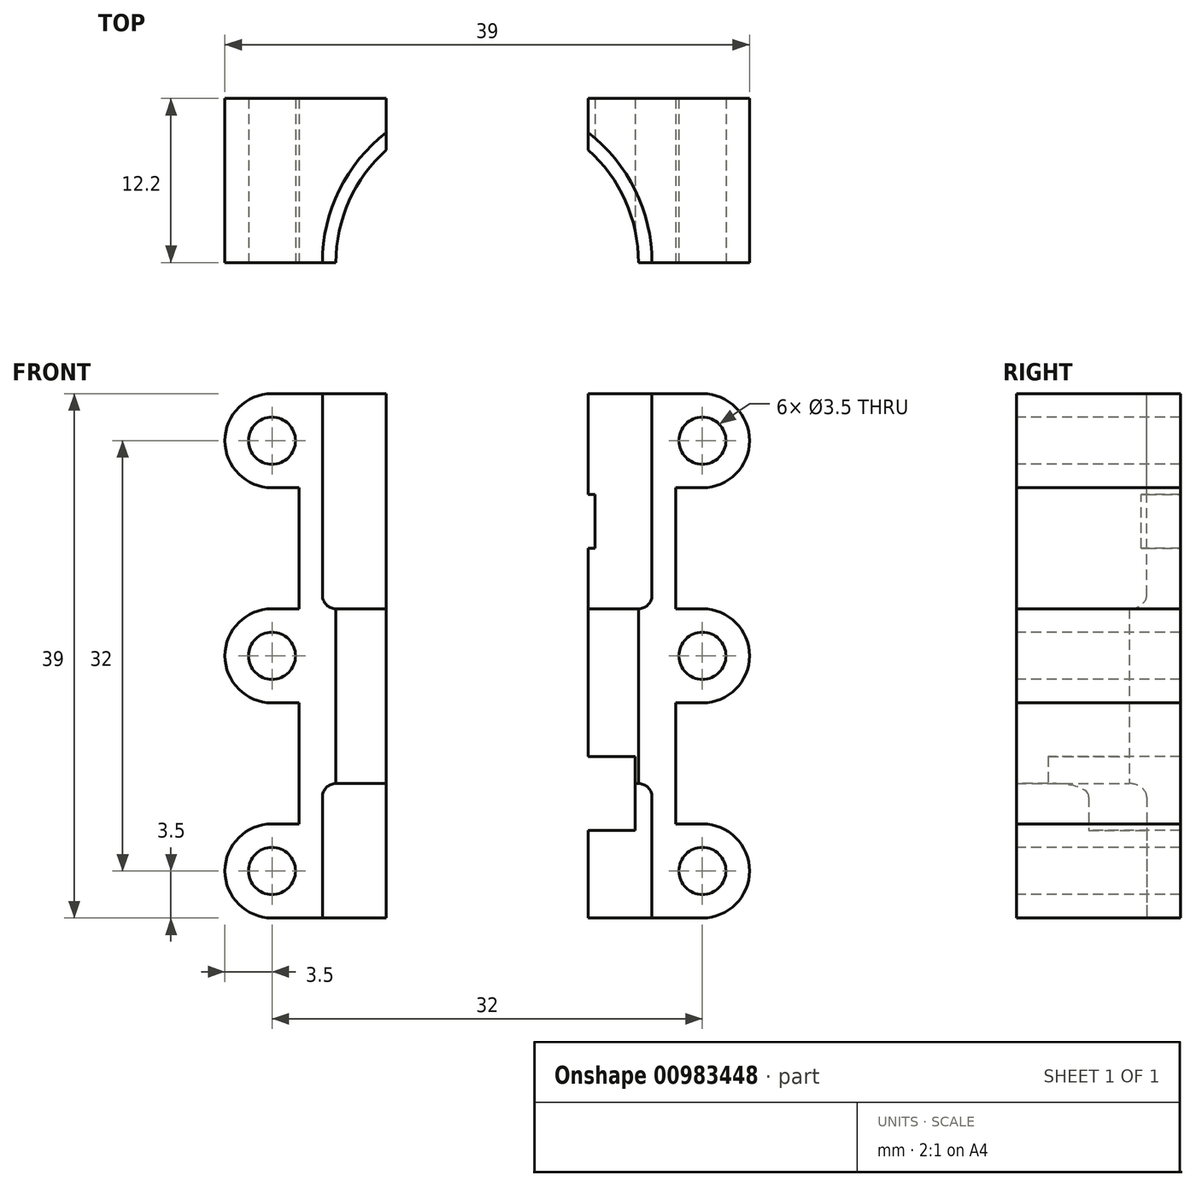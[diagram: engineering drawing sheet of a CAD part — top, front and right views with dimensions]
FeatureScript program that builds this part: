
annotation { "Feature Type Name" : "Feature", "Feature Type Description" : "" }
export const myFeature = defineFeature(function(context is Context, id is Id, definition is map)
    precondition{}
    {
        {
            var Q0;
            Q0=qCreatedBy(makeId("Top.planeOp"),FACE);
            var sketch = newSketch(context, id + "F0", { "sketchPlane" : qUnion([Q0])});
            skCircle(sketch, "E0", {"center": v(0, 0) * mm, "radius": 11.25 * mm});
            skSolve(sketch);
        }
        {
            var Q0;
            Q0=qSketchRegion(id+"F0",true);
            extrude(context, id + "F1", {"entities" : qUnion([Q0]), "depth" : 39 * mm, "offsetDistance" : 25 * mm});
        }
        {
            var Q0;
            Q0=makeQuery(id+"F1.opExtrude","CAP_FACE",FACE,{"disambiguationData":[OSD([sQuery(id+"F0.wireOp",EDGE,"E0")])],"isStart":false});
            var sketch = newSketch(context, id + "F2", { "sketchPlane" : qUnion([Q0])});
            skCircle(sketch, "E1", {"center": v(0, 0) * mm, "radius": 12.25 * mm});
            skSolve(sketch);
        }
        {
            var Q0;
            Q0=makeQuery(id+"F2.imprint","IMPRINT",FACE,{"disambiguationData":[TD([[makeQuery(id+"F2.imprint","IMPRINT",EDGE,{"derivedFrom":sQuery(id+"F2.wireOp",EDGE,"E1")}),1.0]])]});
            extrude(context, id + "F3", {"entities" : qUnion([Q0]), "operationType" : NewBodyOperationType.ADD, "oppositeDirection" : true, "depth" : 16 * mm, "offsetDistance" : 25 * mm});
        }
        {
            var Q0;
            Q0=makeQuery(id+"F1.opExtrude","CAP_FACE",FACE,{"disambiguationData":[OSD([sQuery(id+"F0.wireOp",EDGE,"E0")])],"isStart":true});
            var sketch = newSketch(context, id + "F4", { "sketchPlane" : qUnion([Q0])});
            skCircle(sketch, "E2", {"center": v(0, 0) * mm, "radius": 12.25 * mm});
            skSolve(sketch);
        }
        {
            var Q0;
            Q0=makeQuery(id+"F3.opExtrude","CAP_EDGE",EDGE,{"disambiguationData":[OSD([sQuery(id+"F2.wireOp",EDGE,"E1")])],"isStart":false});
            fillet(context, id + "F5", {"entities" : qUnion([Q0]), "radius" : 1 * mm, "tangentPropagation" : true, "allowEdgeOverflow" : false});
        }
        {
            var Q0;
            Q0=makeQuery(id+"F4.imprint","IMPRINT",FACE,{"disambiguationData":[TD([[makeQuery(id+"F4.imprint","IMPRINT",EDGE,{"derivedFrom":sQuery(id+"F4.wireOp",EDGE,"E2")}),1.0]])]});
            extrude(context, id + "F6", {"entities" : qUnion([Q0]), "operationType" : NewBodyOperationType.ADD, "oppositeDirection" : true, "depth" : 10 * mm, "offsetDistance" : 25 * mm});
        }
        {
            var Q0;
            Q0=makeQuery(id+"F6.opExtrude","CAP_EDGE",EDGE,{"disambiguationData":[OSD([sQuery(id+"F4.wireOp",EDGE,"E2")])],"isStart":false});
            fillet(context, id + "F7", {"entities" : qUnion([Q0]), "radius" : 1 * mm, "tangentPropagation" : true, "allowEdgeOverflow" : false});
        }
        {
            var Q0;
            {var subQ0=sQuery(id+"F0.wireOp",EDGE,"E0");Q0=makeQuery(id+"F6.boolean.opBoolean","MERGE",FACE,{"derivedFrom":[makeQuery(id+"F1.opExtrude","CAP_FACE",FACE,{"disambiguationData":[OSD([subQ0])],"isStart":true}),makeQuery(id+"F6.opExtrude","CAP_FACE",FACE,{"disambiguationData":[OSD([subQ0,sQuery(id+"F4.wireOp",EDGE,"E2")])],"isStart":true})]});}
            var sketch = newSketch(context, id + "F8", { "sketchPlane" : qUnion([Q0])});
            skLineSegment(sketch, "E3.bottom", {"start": v(-5.5, 12.25) * mm, "end": v(5.5, 12.25) * mm});
            skLineSegment(sketch, "E3.top", {"start": v(-5.5, 10.25) * mm, "end": v(5.5, 10.25) * mm});
            skLineSegment(sketch, "E3.left", {"start": v(-5.5, 12.25) * mm, "end": v(-5.5, 10.25) * mm});
            skLineSegment(sketch, "E3.right", {"start": v(5.5, 12.25) * mm, "end": v(5.5, 10.25) * mm});
            skPoint(sketch, "E3.middle", {"position": v(0, 11.25) * mm});
            skSolve(sketch);
        }
        {
            var Q0;
            {var subQ0=sQuery(id+"F8.wireOp",EDGE,"E3.left");var subQ1=sQuery(id+"F8.wireOp",EDGE,"E3.bottom");var subQ2=makeQuery(id+"F8.imprint","INTERSECT",VERTEX,{"derivedFrom":[subQ1,subQ0]});Q0=makeQuery(id+"F8.imprint","IMPRINT",FACE,{"disambiguationData":[TD([[makeQuery(id+"F8.imprint","IMPRINT",EDGE,{"disambiguationData":[TD([[subQ2,-1.0]])],"derivedFrom":subQ1}),-1.0]])]});}
            var Q1;
            {var subQ0=sQuery(id+"F8.wireOp",EDGE,"E3.right");var subQ1=sQuery(id+"F8.wireOp",EDGE,"E3.bottom");var subQ2=makeQuery(id+"F8.imprint","INTERSECT",VERTEX,{"derivedFrom":[subQ1,subQ0]});Q1=makeQuery(id+"F8.imprint","IMPRINT",FACE,{"disambiguationData":[TD([[makeQuery(id+"F8.imprint","IMPRINT",EDGE,{"disambiguationData":[TD([[subQ2,1.0]])],"derivedFrom":subQ1}),-1.0]])]});}
            extrude(context, id + "F9", {"entities" : qUnion([Q0, Q1]), "operationType" : NewBodyOperationType.ADD, "oppositeDirection" : true, "depth" : 9 * mm, "offsetDistance" : 25 * mm});
        }
        {
            var Q0;
            {var subQ0=sQuery(id+"F8.wireOp",EDGE,"E3.bottom");var subQ1=sQuery(id+"F4.wireOp",EDGE,"E2");var subQ2=sQuery(id+"F0.wireOp",EDGE,"E0");Q0=makeQuery(id+"F9.boolean.opBoolean","MERGE",FACE,{"derivedFrom":[makeQuery(id+"F6.boolean.opBoolean","MERGE",FACE,{"derivedFrom":[makeQuery(id+"F1.opExtrude","CAP_FACE",FACE,{"disambiguationData":[OSD([subQ2])],"isStart":true}),makeQuery(id+"F6.opExtrude","CAP_FACE",FACE,{"disambiguationData":[OSD([subQ2,subQ1])],"isStart":true})]}),makeQuery(id+"F9.opExtrude","CAP_FACE",FACE,{"disambiguationData":[OSD([subQ1,subQ0,sQuery(id+"F8.wireOp",EDGE,"E3.left")])],"isStart":true}),makeQuery(id+"F9.opExtrude","CAP_FACE",FACE,{"disambiguationData":[OSD([subQ1,subQ0,sQuery(id+"F8.wireOp",EDGE,"E3.right")])],"isStart":true})]});}
            var sketch = newSketch(context, id + "F10", { "sketchPlane" : qUnion([Q0])});
            skLineSegment(sketch, "E4.bottom", {"start": v(-7.5, -8.25) * mm, "end": v(7.5, -8.25) * mm});
            skLineSegment(sketch, "E4.top", {"start": v(-7.5, -12.25) * mm, "end": v(7.5, -12.25) * mm});
            skLineSegment(sketch, "E4.left", {"start": v(-7.5, -8.25) * mm, "end": v(-7.5, -12.25) * mm});
            skLineSegment(sketch, "E4.right", {"start": v(7.5, -8.25) * mm, "end": v(7.5, -12.25) * mm});
            skPoint(sketch, "E4.middle", {"position": v(0, -10.25) * mm});
            skSolve(sketch);
        }
        {
            var Q0;
            {var subQ0=sQuery(id+"F10.wireOp",EDGE,"E4.right");var subQ1=sQuery(id+"F10.wireOp",EDGE,"E4.top");var subQ2=makeQuery(id+"F10.imprint","INTERSECT",VERTEX,{"derivedFrom":[subQ1,subQ0]});Q0=makeQuery(id+"F10.imprint","IMPRINT",FACE,{"disambiguationData":[TD([[makeQuery(id+"F10.imprint","IMPRINT",EDGE,{"disambiguationData":[TD([[subQ2,1.0]])],"derivedFrom":subQ1}),1.0]])]});}
            var Q1;
            {var subQ0=sQuery(id+"F10.wireOp",EDGE,"E4.left");var subQ1=sQuery(id+"F10.wireOp",EDGE,"E4.top");var subQ2=makeQuery(id+"F10.imprint","INTERSECT",VERTEX,{"derivedFrom":[subQ1,subQ0]});Q1=makeQuery(id+"F10.imprint","IMPRINT",FACE,{"disambiguationData":[TD([[makeQuery(id+"F10.imprint","IMPRINT",EDGE,{"disambiguationData":[TD([[subQ2,-1.0]])],"derivedFrom":subQ1}),1.0]])]});}
            var Q2;
            {var subQ4=sQuery(id+"F10.wireOp",EDGE,"E4.bottom");Q2=makeQuery(id+"F10.imprint","IMPRINT",FACE,{"disambiguationData":[TD([[makeQuery(id+"F10.imprint","IMPRINT",EDGE,{"derivedFrom":subQ4}),-1.0]])]});}
            extrude(context, id + "F11", {"entities" : qUnion([Q0, Q1, Q2]), "operationType" : NewBodyOperationType.ADD, "oppositeDirection" : true, "depth" : 39 * mm, "offsetDistance" : 25 * mm});
        }
        {
            var Q0;
            Q0=makeQuery(id+"F11.opExtrude","SWEPT_FACE",FACE,{"disambiguationData":[OSD([sQuery(id+"F10.wireOp",EDGE,"E4.top")])]});
            var sketch = newSketch(context, id + "F12", { "sketchPlane" : qUnion([Q0])});
            skLineSegment(sketch, "E5.bottom", {"start": v(-11, 12) * mm, "end": v(-7.5, 12) * mm});
            skLineSegment(sketch, "E5.top", {"start": v(-11, 6.5) * mm, "end": v(-7.5, 6.5) * mm});
            skLineSegment(sketch, "E5.left", {"start": v(-11, 12) * mm, "end": v(-11, 6.5) * mm});
            skLineSegment(sketch, "E5.right", {"start": v(-7.5, 12) * mm, "end": v(-7.5, 6.5) * mm});
            skSolve(sketch);
        }
        {
            var Q0;
            Q0=makeQuery(id+"F12.imprint","IMPRINT",FACE,{"disambiguationData":[TD([[makeQuery(id+"F12.imprint","IMPRINT",EDGE,{"derivedFrom":sQuery(id+"F12.wireOp",EDGE,"E5.bottom")}),-1.0]])]});
            extrude(context, id + "F13", {"entities" : qUnion([Q0]), "operationType" : NewBodyOperationType.ADD, "depth" : 2 * mm, "offsetDistance" : 25 * mm, "hasSecondDirection" : true, "secondDirectionOppositeDirection" : true, "secondDirectionDepth" : 12 * mm});
        }
        {
            var Q0;
            Q0=makeQuery(id+"F11.opExtrude","SWEPT_FACE",FACE,{"disambiguationData":[OSD([sQuery(id+"F10.wireOp",EDGE,"E4.top")])]});
            var sketch = newSketch(context, id + "F14", { "sketchPlane" : qUnion([Q0])});
            skCircle(sketch, "E6", {"center": v(-0.06, 19) * mm, "radius": 6.5 * mm});
            skSolve(sketch);
        }
        {
            var Q0;
            Q0=makeQuery(id+"F14.imprint","IMPRINT",FACE,{"disambiguationData":[TD([[makeQuery(id+"F14.imprint","IMPRINT",EDGE,{"derivedFrom":sQuery(id+"F14.wireOp",EDGE,"E6")}),1.0]])]});
            extrude(context, id + "F15", {"entities" : qUnion([Q0]), "operationType" : NewBodyOperationType.ADD, "depth" : 2 * mm, "offsetDistance" : 25 * mm});
        }
        {
            var Q0;
            Q0=makeQuery(id+"F11.opExtrude","SWEPT_FACE",FACE,{"disambiguationData":[OSD([sQuery(id+"F10.wireOp",EDGE,"E4.top")])]});
            var sketch = newSketch(context, id + "F16", { "sketchPlane" : qUnion([Q0])});
            skLineSegment(sketch, "E7.bottom", {"start": v(-8, 27.5) * mm, "end": v(-4.5, 27.5) * mm});
            skLineSegment(sketch, "E7.top", {"start": v(-8, 31.5) * mm, "end": v(-4.5, 31.5) * mm});
            skLineSegment(sketch, "E7.left", {"start": v(-8, 27.5) * mm, "end": v(-8, 31.5) * mm});
            skLineSegment(sketch, "E7.right", {"start": v(-4.5, 27.5) * mm, "end": v(-4.5, 31.5) * mm});
            skSolve(sketch);
        }
        {
            var Q0;
            Q0=makeQuery(id+"F16.imprint","IMPRINT",FACE,{"disambiguationData":[TD([[makeQuery(id+"F16.imprint","IMPRINT",EDGE,{"derivedFrom":sQuery(id+"F16.wireOp",EDGE,"E7.bottom")}),1.0]])]});
            var Q1;
            {var subQ2=sQuery(id+"F16.wireOp",EDGE,"E7.right");Q1=makeQuery(id+"F16.imprint","IMPRINT",FACE,{"disambiguationData":[TD([[makeQuery(id+"F16.imprint","IMPRINT",EDGE,{"derivedFrom":subQ2}),1.0]])]});}
            extrude(context, id + "F17", {"entities" : qUnion([Q0, Q1]), "operationType" : NewBodyOperationType.ADD, "depth" : 6 * mm, "offsetDistance" : 25 * mm, "hasSecondDirection" : true, "secondDirectionOppositeDirection" : true, "secondDirectionDepth" : 16.7 * mm});
        }
        {
            var Q0;
            Q0=qCreatedBy(makeId("Front.planeOp"),FACE);
            var sketch = newSketch(context, id + "F18", { "sketchPlane" : qUnion([Q0])});
            skLineSegment(sketch, "E8.bottom", {"start": v(14, 0) * mm, "end": v(-14, 0) * mm});
            skLineSegment(sketch, "E8.top", {"start": v(14, 39) * mm, "end": v(-14, 39) * mm});
            skLineSegment(sketch, "E8.left", {"start": v(14, 0) * mm, "end": v(14, 39) * mm});
            skLineSegment(sketch, "E8.right", {"start": v(-14, 0) * mm, "end": v(-14, 39) * mm});
            skPoint(sketch, "E8.middle", {"position": v(0, 19.5) * mm});
            skSolve(sketch);
        }
        {
            var Q0;
            Q0=makeQuery(id+"F18.imprint","IMPRINT",FACE,{"disambiguationData":[TD([[makeQuery(id+"F18.imprint","IMPRINT",EDGE,{"derivedFrom":sQuery(id+"F18.wireOp",EDGE,"E8.bottom")}),-1.0]])]});
            extrude(context, id + "F19", {"entities" : qUnion([Q0]), "depth" : 13.5 * mm, "offsetDistance" : 25 * mm, "hasSecondDirection" : true, "secondDirectionOppositeDirection" : true, "secondDirectionDepth" : 12.2 * mm});
        }
        {
            var Q0;
            Q0=makeQuery(id+"F1.opExtrude","SWEPT_BODY",BODY,{"disambiguationData":[OSD([sQuery(id+"F0.wireOp",EDGE,"E0")])]});
            var Q1;
            Q1=makeQuery(id+"F19.opExtrude","SWEPT_BODY",BODY,{"disambiguationData":[OSD([sQuery(id+"F18.wireOp",EDGE,"E8.bottom"),sQuery(id+"F18.wireOp",EDGE,"E8.top"),sQuery(id+"F18.wireOp",EDGE,"E8.left"),sQuery(id+"F18.wireOp",EDGE,"E8.right")])]});
            booleanBodies(context, id + "F20", {"operationType" : BooleanOperationType.SUBTRACTION, "tools" : qUnion([Q0]), "targets" : qUnion([Q1])});
        }
        {
            var Q0;
            Q0=makeQuery(id+"F19.opExtrude","CAP_FACE",FACE,{"disambiguationData":[OSD([sQuery(id+"F18.wireOp",EDGE,"E8.bottom"),sQuery(id+"F18.wireOp",EDGE,"E8.top"),sQuery(id+"F18.wireOp",EDGE,"E8.left"),sQuery(id+"F18.wireOp",EDGE,"E8.right")])],"isStart":false});
            var sketch = newSketch(context, id + "F21", { "sketchPlane" : qUnion([Q0])});
            skLineSegment(sketch, "E9.bottom", {"start": v(16, 7) * mm, "end": v(-16, 7) * mm});
            skLineSegment(sketch, "E9.top", {"start": v(16, 0) * mm, "end": v(-16, 0) * mm});
            skLineSegment(sketch, "E9.left", {"start": v(19.5, 3.5) * mm, "end": v(19.5, 3.5) * mm});
            skLineSegment(sketch, "E9.right", {"start": v(-19.5, 3.5) * mm, "end": v(-19.5, 3.5) * mm});
            skPoint(sketch, "E9.middle", {"position": v(0, 3.5) * mm});
            skLineSegment(sketch, "E10.bottom", {"start": v(16, 39) * mm, "end": v(-16, 39) * mm});
            skLineSegment(sketch, "E10.top", {"start": v(16, 32) * mm, "end": v(-16, 32) * mm});
            skLineSegment(sketch, "E10.left", {"start": v(19.5, 35.5) * mm, "end": v(19.5, 35.5) * mm});
            skLineSegment(sketch, "E10.right", {"start": v(-19.5, 35.5) * mm, "end": v(-19.5, 35.5) * mm});
            skPoint(sketch, "E10.middle", {"position": v(0, 35.5) * mm});
            skPoint(sketch, "E11.visualSharp", {"position": v(-19.5, 0) * mm});
            skArc(sketch, "E11.filletArc", {"start": v(-19.5, 3.5) * mm, "mid": v(-18.47, 1.03) * mm, "end": v(-16, 0) * mm});
            skPoint(sketch, "E12.visualSharp", {"position": v(-19.5, 7) * mm});
            skArc(sketch, "E12.filletArc", {"start": v(-16, 7) * mm, "mid": v(-18.47, 5.97) * mm, "end": v(-19.5, 3.5) * mm});
            skPoint(sketch, "E13.visualSharp", {"position": v(-19.5, 32) * mm});
            skArc(sketch, "E13.filletArc", {"start": v(-19.5, 35.5) * mm, "mid": v(-18.47, 33.03) * mm, "end": v(-16, 32) * mm});
            skPoint(sketch, "E14.visualSharp", {"position": v(19.5, 39) * mm});
            skArc(sketch, "E14.filletArc", {"start": v(19.5, 35.5) * mm, "mid": v(18.47, 37.97) * mm, "end": v(16, 39) * mm});
            skPoint(sketch, "E15.visualSharp", {"position": v(19.5, 32) * mm});
            skArc(sketch, "E15.filletArc", {"start": v(16, 32) * mm, "mid": v(18.47, 33.03) * mm, "end": v(19.5, 35.5) * mm});
            skPoint(sketch, "E16.visualSharp", {"position": v(19.5, 0) * mm});
            skArc(sketch, "E16.filletArc", {"start": v(16, 0) * mm, "mid": v(18.47, 1.03) * mm, "end": v(19.5, 3.5) * mm});
            skPoint(sketch, "E17.visualSharp", {"position": v(-19.5, 39) * mm});
            skArc(sketch, "E17.filletArc", {"start": v(-16, 39) * mm, "mid": v(-18.47, 37.97) * mm, "end": v(-19.5, 35.5) * mm});
            skPoint(sketch, "E18.visualSharp", {"position": v(19.5, 7) * mm});
            skArc(sketch, "E18.filletArc", {"start": v(19.5, 3.5) * mm, "mid": v(18.47, 5.97) * mm, "end": v(16, 7) * mm});
            skCircle(sketch, "E19", {"center": v(-16, 35.5) * mm, "radius": 1.75 * mm});
            skCircle(sketch, "E20", {"center": v(16, 35.5) * mm, "radius": 1.75 * mm});
            skCircle(sketch, "E21", {"center": v(16, 3.5) * mm, "radius": 1.75 * mm});
            skCircle(sketch, "E22", {"center": v(-16, 3.5) * mm, "radius": 1.75 * mm});
            skLineSegment(sketch, "E23.bottom", {"start": v(16, 16) * mm, "end": v(-16, 16) * mm});
            skLineSegment(sketch, "E23.top", {"start": v(16, 23) * mm, "end": v(-16, 23) * mm});
            skLineSegment(sketch, "E23.left", {"start": v(19.5, 19.5) * mm, "end": v(19.5, 19.5) * mm});
            skLineSegment(sketch, "E23.right", {"start": v(-19.5, 19.5) * mm, "end": v(-19.5, 19.5) * mm});
            skPoint(sketch, "E23.middle", {"position": v(0, 19.5) * mm});
            skPoint(sketch, "E24.visualSharp", {"position": v(-19.5, 23) * mm});
            skArc(sketch, "E24.filletArc", {"start": v(-16, 23) * mm, "mid": v(-18.47, 21.97) * mm, "end": v(-19.5, 19.5) * mm});
            skPoint(sketch, "E25.visualSharp", {"position": v(-19.5, 16) * mm});
            skArc(sketch, "E25.filletArc", {"start": v(-19.5, 19.5) * mm, "mid": v(-18.47, 17.03) * mm, "end": v(-16, 16) * mm});
            skPoint(sketch, "E26.visualSharp", {"position": v(19.5, 16) * mm});
            skArc(sketch, "E26.filletArc", {"start": v(16, 16) * mm, "mid": v(18.47, 17.03) * mm, "end": v(19.5, 19.5) * mm});
            skPoint(sketch, "E27.visualSharp", {"position": v(19.5, 23) * mm});
            skArc(sketch, "E27.filletArc", {"start": v(19.5, 19.5) * mm, "mid": v(18.47, 21.97) * mm, "end": v(16, 23) * mm});
            skCircle(sketch, "E28", {"center": v(-16, 19.5) * mm, "radius": 1.75 * mm});
            skCircle(sketch, "E29", {"center": v(16, 19.5) * mm, "radius": 1.75 * mm});
            skSolve(sketch);
        }
        {
            var Q0;
            {var subQ0=sQuery(id+"F21.wireOp",EDGE,"E11.filletArc");Q0=makeQuery(id+"F21.imprint","IMPRINT",FACE,{"disambiguationData":[TD([[makeQuery(id+"F21.imprint","IMPRINT",EDGE,{"derivedFrom":subQ0}),1.0]])]});}
            var Q1;
            {var subQ5=sQuery(id+"F21.wireOp",EDGE,"E13.filletArc");Q1=makeQuery(id+"F21.imprint","IMPRINT",FACE,{"disambiguationData":[TD([[makeQuery(id+"F21.imprint","IMPRINT",EDGE,{"derivedFrom":subQ5}),1.0]])]});}
            var Q2;
            {var subQ5=sQuery(id+"F21.wireOp",EDGE,"E14.filletArc");Q2=makeQuery(id+"F21.imprint","IMPRINT",FACE,{"disambiguationData":[TD([[makeQuery(id+"F21.imprint","IMPRINT",EDGE,{"derivedFrom":subQ5}),1.0]])]});}
            var Q3;
            {var subQ4=sQuery(id+"F21.wireOp",EDGE,"E16.filletArc");Q3=makeQuery(id+"F21.imprint","IMPRINT",FACE,{"disambiguationData":[TD([[makeQuery(id+"F21.imprint","IMPRINT",EDGE,{"derivedFrom":subQ4}),1.0]])]});}
            var Q4;
            {var subQ4=sQuery(id+"F21.wireOp",EDGE,"E24.filletArc");var subQ6=sQuery(id+"F21.wireOp",EDGE,"E25.filletArc");var subQ7=makeQuery(id+"F21.imprint","INTERSECT",VERTEX,{"derivedFrom":[subQ4,subQ6]});Q4=makeQuery(id+"F21.imprint","IMPRINT",FACE,{"disambiguationData":[TD([[makeQuery(id+"F21.imprint","IMPRINT",EDGE,{"disambiguationData":[TD([[subQ7,1.0]])],"derivedFrom":subQ4}),1.0]])]});}
            var Q5;
            {var subQ0=sQuery(id+"F21.wireOp",EDGE,"E26.filletArc");var subQ6=sQuery(id+"F21.wireOp",EDGE,"E27.filletArc");var subQ7=makeQuery(id+"F21.imprint","INTERSECT",VERTEX,{"derivedFrom":[subQ0,subQ6]});Q5=makeQuery(id+"F21.imprint","IMPRINT",FACE,{"disambiguationData":[TD([[makeQuery(id+"F21.imprint","IMPRINT",EDGE,{"disambiguationData":[TD([[subQ7,1.0]])],"derivedFrom":subQ0}),1.0]])]});}
            extrude(context, id + "F22", {"entities" : qUnion([Q0, Q1, Q2, Q3, Q4, Q5]), "operationType" : NewBodyOperationType.ADD, "oppositeDirection" : true, "depth" : 25.7 * mm, "offsetDistance" : 25 * mm});
        }
        {
            var Q0;
            {var subQ0=sQuery(id+"F21.wireOp",EDGE,"E22");var subQ1=makeQuery(id+"F19.opExtrude","CAP_EDGE",EDGE,{"disambiguationData":[OSD([sQuery(id+"F18.wireOp",EDGE,"E8.right")])],"isStart":false});var subQ2=makeQuery(id+"F21.imprint","INTERSECT",VERTEX,{"disambiguationData":[OD(0.0)],"derivedFrom":[subQ1,subQ0]});Q0=makeQuery(id+"F21.imprint","IMPRINT",FACE,{"disambiguationData":[TD([[makeQuery(id+"F21.imprint","IMPRINT",EDGE,{"disambiguationData":[TD([[subQ2,-1.0]])],"derivedFrom":subQ0}),1.0]])]});}
            var Q1;
            {var subQ0=sQuery(id+"F21.wireOp",EDGE,"E21");var subQ1=makeQuery(id+"F19.opExtrude","CAP_EDGE",EDGE,{"disambiguationData":[OSD([sQuery(id+"F18.wireOp",EDGE,"E8.left")])],"isStart":false});var subQ2=makeQuery(id+"F21.imprint","INTERSECT",VERTEX,{"disambiguationData":[OD(0.0)],"derivedFrom":[subQ1,subQ0]});Q1=makeQuery(id+"F21.imprint","IMPRINT",FACE,{"disambiguationData":[TD([[makeQuery(id+"F21.imprint","IMPRINT",EDGE,{"disambiguationData":[TD([[subQ2,1.0]])],"derivedFrom":subQ0}),1.0]])]});}
            var Q2;
            {var subQ0=sQuery(id+"F21.wireOp",EDGE,"E20");var subQ1=makeQuery(id+"F19.opExtrude","CAP_EDGE",EDGE,{"disambiguationData":[OSD([sQuery(id+"F18.wireOp",EDGE,"E8.left")])],"isStart":false});var subQ2=makeQuery(id+"F21.imprint","INTERSECT",VERTEX,{"disambiguationData":[OD(0.0)],"derivedFrom":[subQ1,subQ0]});Q2=makeQuery(id+"F21.imprint","IMPRINT",FACE,{"disambiguationData":[TD([[makeQuery(id+"F21.imprint","IMPRINT",EDGE,{"disambiguationData":[TD([[subQ2,-1.0]])],"derivedFrom":subQ0}),1.0]])]});}
            var Q3;
            {var subQ0=sQuery(id+"F21.wireOp",EDGE,"E19");var subQ1=makeQuery(id+"F19.opExtrude","CAP_EDGE",EDGE,{"disambiguationData":[OSD([sQuery(id+"F18.wireOp",EDGE,"E8.right")])],"isStart":false});var subQ2=makeQuery(id+"F21.imprint","INTERSECT",VERTEX,{"disambiguationData":[OD(0.0)],"derivedFrom":[subQ1,subQ0]});Q3=makeQuery(id+"F21.imprint","IMPRINT",FACE,{"disambiguationData":[TD([[makeQuery(id+"F21.imprint","IMPRINT",EDGE,{"disambiguationData":[TD([[subQ2,1.0]])],"derivedFrom":subQ0}),1.0]])]});}
            var Q4;
            {var subQ0=sQuery(id+"F21.wireOp",EDGE,"E19");var subQ1=makeQuery(id+"F19.opExtrude","CAP_EDGE",EDGE,{"disambiguationData":[OSD([sQuery(id+"F18.wireOp",EDGE,"E8.right")])],"isStart":false});var subQ2=makeQuery(id+"F21.imprint","INTERSECT",VERTEX,{"disambiguationData":[OD(0.0)],"derivedFrom":[subQ1,subQ0]});Q4=makeQuery(id+"F21.imprint","IMPRINT",FACE,{"disambiguationData":[TD([[makeQuery(id+"F21.imprint","IMPRINT",EDGE,{"disambiguationData":[TD([[subQ2,-1.0]])],"derivedFrom":subQ0}),1.0]])]});}
            var Q5;
            {var subQ0=sQuery(id+"F21.wireOp",EDGE,"E28");var subQ1=makeQuery(id+"F19.opExtrude","CAP_EDGE",EDGE,{"disambiguationData":[OSD([sQuery(id+"F18.wireOp",EDGE,"E8.right")])],"isStart":false});var subQ2=makeQuery(id+"F21.imprint","INTERSECT",VERTEX,{"disambiguationData":[OD(0.0)],"derivedFrom":[subQ1,subQ0]});Q5=makeQuery(id+"F21.imprint","IMPRINT",FACE,{"disambiguationData":[TD([[makeQuery(id+"F21.imprint","IMPRINT",EDGE,{"disambiguationData":[TD([[subQ2,1.0]])],"derivedFrom":subQ0}),1.0]])]});}
            var Q6;
            {var subQ0=sQuery(id+"F21.wireOp",EDGE,"E29");var subQ1=makeQuery(id+"F19.opExtrude","CAP_EDGE",EDGE,{"disambiguationData":[OSD([sQuery(id+"F18.wireOp",EDGE,"E8.left")])],"isStart":false});var subQ2=makeQuery(id+"F21.imprint","INTERSECT",VERTEX,{"disambiguationData":[OD(0.0)],"derivedFrom":[subQ1,subQ0]});Q6=makeQuery(id+"F21.imprint","IMPRINT",FACE,{"disambiguationData":[TD([[makeQuery(id+"F21.imprint","IMPRINT",EDGE,{"disambiguationData":[TD([[subQ2,1.0]])],"derivedFrom":subQ0}),1.0]])]});}
            var Q7;
            {var subQ0=sQuery(id+"F21.wireOp",EDGE,"E28");var subQ1=makeQuery(id+"F19.opExtrude","CAP_EDGE",EDGE,{"disambiguationData":[OSD([sQuery(id+"F18.wireOp",EDGE,"E8.right")])],"isStart":false});var subQ2=makeQuery(id+"F21.imprint","INTERSECT",VERTEX,{"disambiguationData":[OD(0.0)],"derivedFrom":[subQ1,subQ0]});Q7=makeQuery(id+"F21.imprint","IMPRINT",FACE,{"disambiguationData":[TD([[makeQuery(id+"F21.imprint","IMPRINT",EDGE,{"disambiguationData":[TD([[subQ2,-1.0]])],"derivedFrom":subQ0}),1.0]])]});}
            extrude(context, id + "F23", {"entities" : qUnion([Q0, Q1, Q2, Q3, Q4, Q5, Q6, Q7]), "operationType" : NewBodyOperationType.REMOVE, "oppositeDirection" : true, "depth" : 25.7 * mm, "offsetDistance" : 25 * mm});
        }
        {
            var Q0;
            {var subQ0=sQuery(id+"F18.wireOp",EDGE,"E8.left");var subQ1=sQuery(id+"F18.wireOp",EDGE,"E8.right");Q0=makeQuery(id+"F22.boolean.opBoolean","MERGE",FACE,{"derivedFrom":[makeQuery(id+"F19.opExtrude","CAP_FACE",FACE,{"disambiguationData":[OSD([sQuery(id+"F18.wireOp",EDGE,"E8.bottom"),sQuery(id+"F18.wireOp",EDGE,"E8.top"),subQ0,subQ1])],"isStart":false}),makeQuery(id+"F22.opExtrude","CAP_FACE",FACE,{"disambiguationData":[OSD([subQ1,sQuery(id+"F21.wireOp",EDGE,"E11.filletArc"),sQuery(id+"F21.wireOp",EDGE,"E12.filletArc"),sQuery(id+"F21.wireOp",EDGE,"E22")])],"isStart":true}),makeQuery(id+"F22.opExtrude","CAP_FACE",FACE,{"disambiguationData":[OSD([subQ1,sQuery(id+"F21.wireOp",EDGE,"E13.filletArc"),sQuery(id+"F21.wireOp",EDGE,"E17.filletArc"),sQuery(id+"F21.wireOp",EDGE,"E19")])],"isStart":true}),makeQuery(id+"F22.opExtrude","CAP_FACE",FACE,{"disambiguationData":[OSD([subQ0,sQuery(id+"F21.wireOp",EDGE,"E14.filletArc"),sQuery(id+"F21.wireOp",EDGE,"E15.filletArc"),sQuery(id+"F21.wireOp",EDGE,"E20")])],"isStart":true}),makeQuery(id+"F22.opExtrude","CAP_FACE",FACE,{"disambiguationData":[OSD([subQ0,sQuery(id+"F21.wireOp",EDGE,"E16.filletArc"),sQuery(id+"F21.wireOp",EDGE,"E18.filletArc"),sQuery(id+"F21.wireOp",EDGE,"E21")])],"isStart":true})]});}
            var sketch = newSketch(context, id + "F24", { "sketchPlane" : qUnion([Q0])});
            skCircle(sketch, "E30", {"center": v(-16, 35.5) * mm, "radius": 4 * mm});
            skCircle(sketch, "E31", {"center": v(16, 35.5) * mm, "radius": 4 * mm});
            skCircle(sketch, "E32", {"center": v(16, 3.5) * mm, "radius": 4 * mm});
            skCircle(sketch, "E33", {"center": v(-16, 3.5) * mm, "radius": 4 * mm});
            skCircle(sketch, "E34", {"center": v(-16, 19.5) * mm, "radius": 4 * mm});
            skCircle(sketch, "E35", {"center": v(16, 19.5) * mm, "radius": 4 * mm});
            skSolve(sketch);
        }
        {
            var Q0;
            {var subQ9=sQuery(id+"F21.wireOp",EDGE,"E19");Q0=makeQuery(id+"F24.imprint","IMPRINT",FACE,{"disambiguationData":[TD([[makeQuery(id+"F24.imprint","IMPRINT",EDGE,{"derivedFrom":makeQuery(id+"F23.boolean.opBoolean","MERGE",EDGE,{"derivedFrom":[makeQuery(id+"F22.opExtrude","CAP_EDGE",EDGE,{"disambiguationData":[OSD([subQ9])],"isStart":true})],"fromTools":[makeQuery(id+"F23.opExtrude","CAP_EDGE",EDGE,{"disambiguationData":[OSD([subQ9])],"isStart":true})]})}),-1.0]])]});}
            var Q1;
            {var subQ7=sQuery(id+"F21.wireOp",EDGE,"E20");Q1=makeQuery(id+"F24.imprint","IMPRINT",FACE,{"disambiguationData":[TD([[makeQuery(id+"F24.imprint","IMPRINT",EDGE,{"derivedFrom":makeQuery(id+"F23.boolean.opBoolean","MERGE",EDGE,{"derivedFrom":[makeQuery(id+"F22.opExtrude","CAP_EDGE",EDGE,{"disambiguationData":[OSD([subQ7])],"isStart":true})],"fromTools":[makeQuery(id+"F23.opExtrude","CAP_EDGE",EDGE,{"disambiguationData":[OSD([subQ7])],"isStart":true})]})}),-1.0]])]});}
            var Q2;
            {var subQ9=sQuery(id+"F21.wireOp",EDGE,"E21");Q2=makeQuery(id+"F24.imprint","IMPRINT",FACE,{"disambiguationData":[TD([[makeQuery(id+"F24.imprint","IMPRINT",EDGE,{"derivedFrom":makeQuery(id+"F23.boolean.opBoolean","MERGE",EDGE,{"derivedFrom":[makeQuery(id+"F22.opExtrude","CAP_EDGE",EDGE,{"disambiguationData":[OSD([subQ9])],"isStart":true})],"fromTools":[makeQuery(id+"F23.opExtrude","CAP_EDGE",EDGE,{"disambiguationData":[OSD([subQ9])],"isStart":true})]})}),-1.0]])]});}
            var Q3;
            {var subQ9=sQuery(id+"F21.wireOp",EDGE,"E22");Q3=makeQuery(id+"F24.imprint","IMPRINT",FACE,{"disambiguationData":[TD([[makeQuery(id+"F24.imprint","IMPRINT",EDGE,{"derivedFrom":makeQuery(id+"F23.boolean.opBoolean","MERGE",EDGE,{"derivedFrom":[makeQuery(id+"F22.opExtrude","CAP_EDGE",EDGE,{"disambiguationData":[OSD([subQ9])],"isStart":true})],"fromTools":[makeQuery(id+"F23.opExtrude","CAP_EDGE",EDGE,{"disambiguationData":[OSD([subQ9])],"isStart":true})]})}),-1.0]])]});}
            var Q4;
            {var subQ6=sQuery(id+"F21.wireOp",EDGE,"E28");Q4=makeQuery(id+"F24.imprint","IMPRINT",FACE,{"disambiguationData":[TD([[makeQuery(id+"F24.imprint","IMPRINT",EDGE,{"derivedFrom":makeQuery(id+"F23.boolean.opBoolean","MERGE",EDGE,{"derivedFrom":[makeQuery(id+"F22.opExtrude","CAP_EDGE",EDGE,{"disambiguationData":[OSD([subQ6])],"isStart":true})],"fromTools":[makeQuery(id+"F23.opExtrude","CAP_EDGE",EDGE,{"disambiguationData":[OSD([subQ6])],"isStart":true})]})}),-1.0]])]});}
            var Q5;
            {var subQ6=sQuery(id+"F21.wireOp",EDGE,"E29");Q5=makeQuery(id+"F24.imprint","IMPRINT",FACE,{"disambiguationData":[TD([[makeQuery(id+"F24.imprint","IMPRINT",EDGE,{"derivedFrom":makeQuery(id+"F23.boolean.opBoolean","MERGE",EDGE,{"derivedFrom":[makeQuery(id+"F22.opExtrude","CAP_EDGE",EDGE,{"disambiguationData":[OSD([subQ6])],"isStart":true})],"fromTools":[makeQuery(id+"F23.opExtrude","CAP_EDGE",EDGE,{"disambiguationData":[OSD([subQ6])],"isStart":true})]})}),-1.0]])]});}
            extrude(context, id + "F25", {"entities" : qUnion([Q0, Q1, Q2, Q3, Q4, Q5]), "operationType" : NewBodyOperationType.REMOVE, "oppositeDirection" : true, "depth" : 2 * mm, "offsetDistance" : 25 * mm});
        }
        {
            var Q0;
            Q0=qCreatedBy(makeId("Front.planeOp"),FACE);
            var sketch = newSketch(context, id + "F26", { "sketchPlane" : qUnion([Q0])});
            skLineSegment(sketch, "E36.bottom", {"start": v(-45.92, -43.17) * mm, "end": v(45.92, -43.17) * mm});
            skLineSegment(sketch, "E36.top", {"start": v(-45.92, 43.17) * mm, "end": v(45.92, 43.17) * mm});
            skLineSegment(sketch, "E36.left", {"start": v(-45.92, -43.17) * mm, "end": v(-45.92, 43.17) * mm});
            skLineSegment(sketch, "E36.right", {"start": v(45.92, -43.17) * mm, "end": v(45.92, 43.17) * mm});
            skPoint(sketch, "E36.middle", {"position": v(0, 0) * mm});
            skSolve(sketch);
        }
        {
            var Q0;
            Q0 = qSketchRegion(id + "F26", true);
            extrude(context, id + "F27", {"entities" : qUnion([Q0]), "operationType" : NewBodyOperationType.REMOVE, "depth" : 42.3 * mm, "offsetDistance" : 25 * mm});
        }
    });
